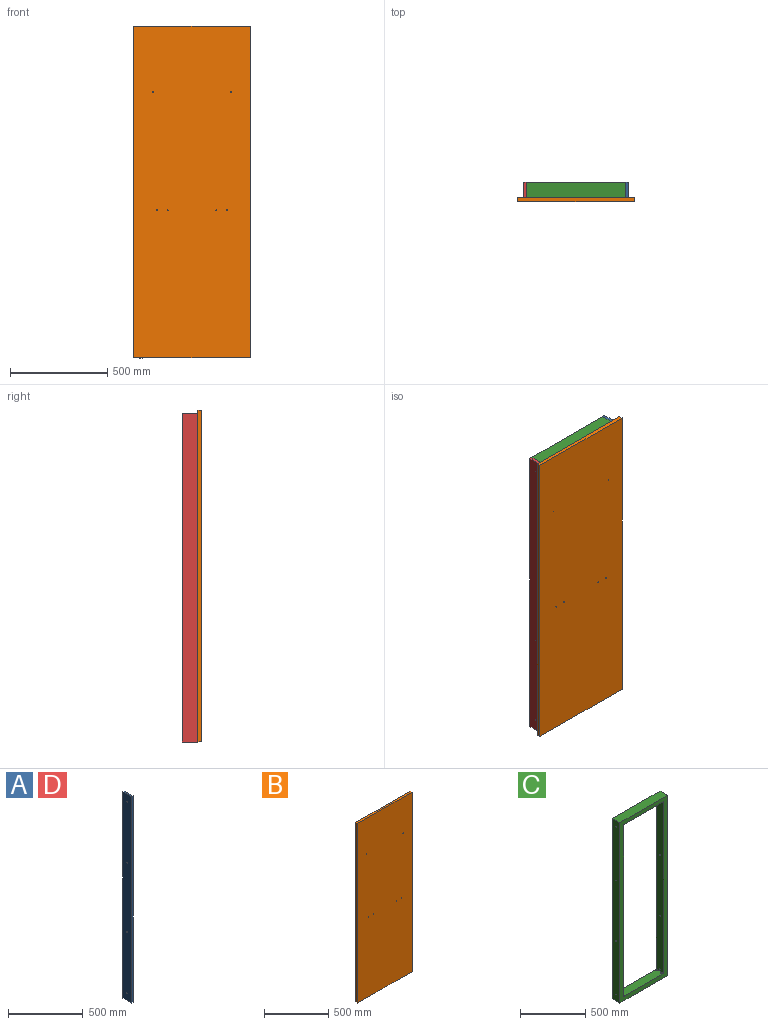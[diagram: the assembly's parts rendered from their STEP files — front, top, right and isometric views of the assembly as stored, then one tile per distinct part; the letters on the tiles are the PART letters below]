
ASSEMBLY  parts=4 mates=3
PART A: 14 faces, bbox 15x80x1690 mm
  f0: plane 1690x80mm, normal (-1,0,0), area 135121.5mm2, adj f1,f2,f3,f4,f6,f8,f10,f12
  f1: plane 80x15mm, normal (0,0,1), area 1200mm2, adj f0,f2,f4,f5
  f2: plane 1690x15mm, normal (0,-1,0), area 25350mm2, adj f0,f1,f3,f5
  f3: plane 80x15mm, normal (0,0,-1), area 1200mm2, adj f0,f2,f4,f5
  f4: plane 1690x15mm, normal (0,1,0), area 25350mm2, adj f0,f1,f3,f5
  f5: plane 1690x80mm, normal (1,0,0), area 135200mm2, adj f1,f2,f3,f4
  f6: cylinder r=2.5mm len=10mm, axis (-1,0,0), area 157.1mm2, adj f0,f7
  f7: plane 5x5mm, normal (-1,0,0), area 19.6mm2, adj f6
  f8: cylinder r=2.5mm len=10mm, axis (-1,0,0), area 157.1mm2, adj f0,f9
  f9: plane 5x5mm, normal (-1,0,0), area 19.6mm2, adj f8
  f10: cylinder r=2.5mm len=10mm, axis (-1,0,0), area 157.1mm2, adj f0,f11
  f11: plane 5x5mm, normal (-1,0,0), area 19.6mm2, adj f10
  f12: cylinder r=2.5mm len=10mm, axis (-1,0,0), area 157.1mm2, adj f0,f13
  f13: plane 5x5mm, normal (-1,0,0), area 19.6mm2, adj f12
PART B: 12 faces, bbox 600x20x1710 mm
  f0: plane 600x20mm, normal (0,0,1), area 12000mm2, adj f1,f8,f10,f11
  f1: plane 1710x20mm, normal (-1,0,0), area 34200mm2, adj f0,f2,f10,f11
  f2: plane 600x20mm, normal (0,0,-1), area 12000mm2, adj f1,f8,f10,f11
  f3: cylinder r=2.5mm len=20mm, axis (0,1,0), area 314.2mm2, adj f10,f11
  f4: cylinder r=2.5mm len=20mm, axis (0,1,0), area 314.2mm2, adj f10,f11
  f5: cylinder r=2.5mm len=20mm, axis (0,1,0), area 314.2mm2, adj f10,f11
  f6: cylinder r=2.5mm len=20mm, axis (0,1,0), area 314.2mm2, adj f10,f11
  f7: cylinder r=2.5mm len=20mm, axis (0,1,0), area 314.2mm2, adj f10,f11
  f8: plane 1710x20mm, normal (1,0,0), area 34200mm2, adj f0,f2,f10,f11
  f9: cylinder r=2.5mm len=20mm, axis (0,1,0), area 314.2mm2, adj f10,f11
  f10: plane 1710x600mm, normal (0,-1,0), area 1025882.2mm2, adj f0,f1,f2,f3,f4,f5,f6,f7
  f11: plane 1710x600mm, normal (0,1,0), area 1025882.2mm2, adj f0,f1,f2,f3,f4,f5,f6,f7
PART C: 22 faces, bbox 515x80x1690 mm
  f0: plane 1610x80mm, normal (1,0,0), area 128721.5mm2, adj f5,f6,f8,f9,f18,f19,f20,f21
  f1: plane 1610x80mm, normal (-1,0,0), area 128721.5mm2, adj f5,f6,f8,f9,f14,f15,f16,f17
  f2: plane 1690x80mm, normal (-1,0,0), area 135121.5mm2, adj f4,f7,f8,f9,f18,f19,f20,f21
  f3: plane 1690x80mm, normal (1,0,0), area 135121.5mm2, adj f4,f7,f8,f9,f14,f15,f16,f17
  f4: plane 515x80mm, normal (0,0,-1), area 40885.8mm2, adj f2,f3,f8,f9,f10,f11,f12,f13
  f5: plane 435x80mm, normal (0,0,1), area 34485.8mm2, adj f0,f1,f8,f9,f10,f11,f12,f13
  f6: plane 435x80mm, normal (0,0,-1), area 34800mm2, adj f0,f1,f8,f9
  f7: plane 515x80mm, normal (0,0,1), area 41200mm2, adj f2,f3,f8,f9
  f8: plane 1690x515mm, normal (0,-1,0), area 170000mm2, adj f0,f1,f2,f3,f4,f5,f6,f7
  f9: plane 1690x515mm, normal (0,1,0), area 170000mm2, adj f0,f1,f2,f3,f4,f5,f6,f7
  f10: cylinder r=5mm len=40mm, axis (0,0,-1), area 1256.6mm2, adj f4,f5
  f11: cylinder r=5mm len=40mm, axis (0,0,-1), area 1256.6mm2, adj f4,f5
  f12: cylinder r=5mm len=40mm, axis (0,0,-1), area 1256.6mm2, adj f4,f5
  f13: cylinder r=5mm len=40mm, axis (0,0,-1), area 1256.6mm2, adj f4,f5
  f14: cylinder r=2.5mm len=40mm, axis (1,0,0), area 628.3mm2, adj f1,f3
  f15: cylinder r=2.5mm len=40mm, axis (1,0,0), area 628.3mm2, adj f1,f3
  f16: cylinder r=2.5mm len=40mm, axis (1,0,0), area 628.3mm2, adj f1,f3
  f17: cylinder r=2.5mm len=40mm, axis (1,0,0), area 628.3mm2, adj f1,f3
  f18: cylinder r=2.5mm len=40mm, axis (1,0,0), area 628.3mm2, adj f0,f2
  f19: cylinder r=2.5mm len=40mm, axis (1,0,0), area 628.3mm2, adj f0,f2
  f20: cylinder r=2.5mm len=40mm, axis (1,0,0), area 628.3mm2, adj f0,f2
  f21: cylinder r=2.5mm len=40mm, axis (1,0,0), area 628.3mm2, adj f0,f2
PART D: same geometry as A
PLACE A t=(211.48,28.76,83)mm
PLACE B t=(-46.02,-11.24,93)mm
PLACE C t=(-46.02,68.76,83)mm
PLACE D rot(axis=(0,0,1),180deg) t=(-303.52,28.76,83)mm
MATE cylindrical A.f12 <-> C.f15  axis (-1,0,0) through (211.48,28.76,868)mm
MATE planar B.f11 <-> C.f8  axis (0,1,0) through (-46.02,-11.24,-762)mm
MATE cylindrical D.f12 <-> C.f15  axis (1,0,0) through (-303.52,28.76,868)mm
